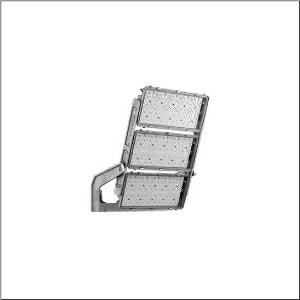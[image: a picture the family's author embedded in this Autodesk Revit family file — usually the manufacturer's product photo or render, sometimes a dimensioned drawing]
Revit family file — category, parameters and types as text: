
# Revit family: floodlight_fl_11_maxi_pro_remote___pl64_5xa779524e01aa_eec4
name_source: partatom
category: Lighting Fixtures
units: mm (PartAtom-declared; Revit-internal decimal feet)

## family parameters
Cut with Voids When Loaded = No
Host = Face
Light Source = No
Part Type = Normal
Room Calculation Point = No
Round Connector Dimension = Use Diameter
Shared = No

## types (1)
- --- (1 x LED, 128450 lm, 1334.7 W, 5700K)
    Apparent Load = 1335 VA
    CIE Flux Codes = 28 80 98 100 100
    Color Rendering = 90
    Color Temperature = 5700K
    Default Elevation = 1800 mm
    Description = Floodlight FL 11  maxi  pro Remote floodlight; light control with lens of PMMA; cover panel of toughened safety glass, transparent; light distribution: PL64, asymmetric direct distribution, LEDcolour temperature: 5700K, rated luminous flux: 128.450lm, colour rendering: CRI > 90, light colour: 957; luminous efficacy: 96lm/W; brightness control: DMX+RDM; with terminal, 6-pole, max. 2.5mm², mains connection: 220..240V/380..400V AC, 50/60Hz, surge voltage resistance: line to ground: 10kV, ECG replaceable separately, no afterglow with DALI off / DMX off command, LED unit replaceable without ESD environment, dustproof LED module, dimming range 10..100%; 1335W reduction: 534W; floodlight with 3x LED unit of diecast aluminium, coated grey; length: 713mm / width: 651mm / height: 338mm; housing frame, of diecast aluminium, uncoated, natural, mounting bracket, of diecast aluminium, uncoated, natural, equipment: Power, protection rating (complete): IP66; insulation class (complete): insulation class I (protective earthing); certification: CE, ENEC, VDE; ball protection: ball impact resistance with accessories, only for outdoor installations, rated ambient temperature 10°C, permissible operating ambient temperature: -40..+30°C, permissible storage temperature: -40..+85°C; packaging unit: 1 piece

Light Distribution: PL64
    Height = 320 mm
    Lamp = 1 x LED
    Lamp Light Flux = 128450 lm
    Lamp Power = 1334.7 W
    Lamp count = 1
    Length = 1002 mm
    Luminous efficacy = 96 lm/W
    Manufacturer = Siteco
    ModVariant = No
    Model = 5XA779524E01AA
    Number of Poles = 1
    OnlyDefault = Yes
    Power Factor = 1
    Product Name = Floodlight FL 11 maxi pro Remote | PL64
    Product group = floodlight | pylon top
    ProductGroupID = 6101
    Protection Class = Protection class I
    Protection Degree = IP 66
    RLX_Detail_Level = 1
    RlxData = <blob elided: 52445 chars, md5=0d6c98b3>
    Socket = socket
    Standby Power = 0 W
    System Light Flux = 128450 lm
    System Power = 1335 W
    Type Comments = factory setting: luminous flux: 100 % | dim-lin: 255 | 920 mA
    Type Image = l_1006784.jpg
    URL = http://relux.com
    VarID = @adj_006917
    Voltage = 0 V
    Weight = 0.00 kg
    Width = 655 mm

## geometry (parser evidence)
native form markers: Blend x4, Sweep x14
no freeform markers — native parametric forms only
